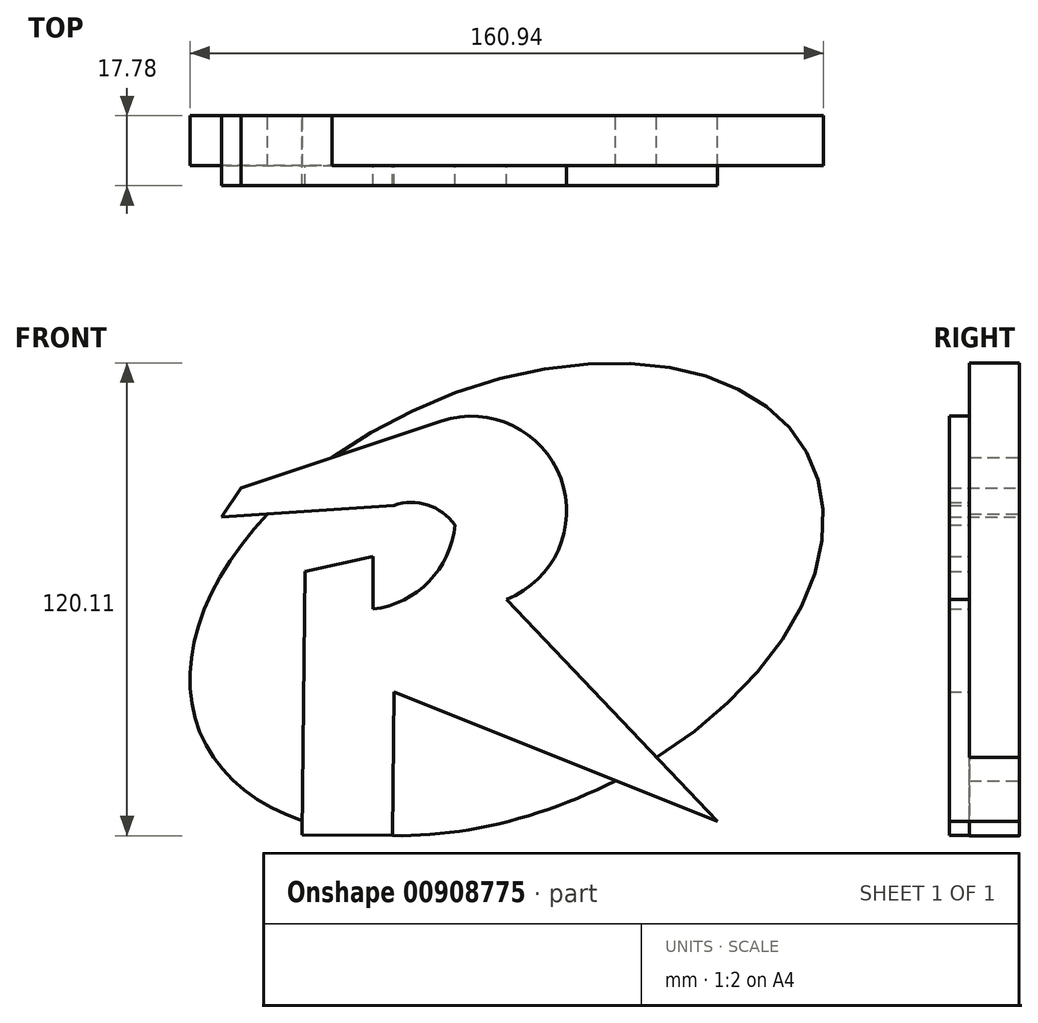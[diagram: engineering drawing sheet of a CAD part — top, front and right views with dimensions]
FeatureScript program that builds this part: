
annotation { "Feature Type Name" : "Feature", "Feature Type Description" : "" }
export const myFeature = defineFeature(function(context is Context, id is Id, definition is map)
    precondition{}
    {
        {
            var Q0;
            Q0=qCreatedBy(makeId("Front.planeOp"),FACE);
            var sketch = newSketch(context, id + "F0", { "sketchPlane" : qUnion([Q0])});
            skEllipse(sketch, "E0", {"center": v(0, 8.22) * mm, "majorRadius": 84.94 * mm, "minorRadius": 53.54 * mm, "majorAxis": v(-0.91, -0.41)});
            skLineSegment(sketch, "E1", {"start": v(-51.94, -51.6) * mm, "end": v(-29.03, -51.82) * mm});
            skLineSegment(sketch, "E2", {"start": v(-51.94, -51.6) * mm, "end": v(-51.3, 15.35) * mm});
            skLineSegment(sketch, "E3", {"start": v(-51.3, 15.35) * mm, "end": v(-33.96, 19.07) * mm});
            skLineSegment(sketch, "E4", {"start": v(-33.96, 19.07) * mm, "end": v(-33.96, 5.74) * mm});
            skArc(sketch, "E5", {"start": v(-33.96, 5.74) * mm, "mid": v(-19.76, 12.74) * mm, "end": v(-13.18, 27.14) * mm});
            skArc(sketch, "E6", {"start": v(-13.18, 27.14) * mm, "mid": v(-20.12, 32.17) * mm, "end": v(-28.69, 32.1) * mm});
            skLineSegment(sketch, "E7", {"start": v(-28.69, 32.1) * mm, "end": v(-72.41, 29.17) * mm});
            skLineSegment(sketch, "E8", {"start": v(-72.41, 29.17) * mm, "end": v(-67.45, 36.44) * mm});
            skLineSegment(sketch, "E9", {"start": v(-67.45, 36.44) * mm, "end": v(-16.6, 53.5) * mm});
            skArc(sketch, "E10", {"start": v(0, 8.22) * mm, "mid": v(13.73, 38.93) * mm, "end": v(-16.6, 53.5) * mm});
            skLineSegment(sketch, "E11", {"start": v(0, 8.22) * mm, "end": v(53.5, -48.22) * mm});
            skLineSegment(sketch, "E12", {"start": v(-29.03, -51.82) * mm, "end": v(-28.67, -15.34) * mm});
            skLineSegment(sketch, "E13", {"start": v(-28.67, -15.34) * mm, "end": v(53.5, -48.22) * mm});
            skSolve(sketch);
        }
        {
            var Q0;
            {var subQ5=sQuery(id+"F0.wireOp",EDGE,"E3");Q0=makeQuery(id+"F0.imprint","IMPRINT",FACE,{"disambiguationData":[TD([[makeQuery(id+"F0.imprint","IMPRINT",EDGE,{"derivedFrom":subQ5}),-1.0]])]});}
            var Q1;
            {var subQ5=sQuery(id+"F0.wireOp",EDGE,"E8");Q1=makeQuery(id+"F0.imprint","IMPRINT",FACE,{"disambiguationData":[TD([[makeQuery(id+"F0.imprint","IMPRINT",EDGE,{"derivedFrom":subQ5}),-1.0]])]});}
            var Q2;
            {var subQ0=sQuery(id+"F0.wireOp",EDGE,"E13");var subQ1=sQuery(id+"F0.wireOp",EDGE,"E0");var subQ2=makeQuery(id+"F0.imprint","INTERSECT",VERTEX,{"derivedFrom":[subQ1,subQ0]});Q2=makeQuery(id+"F0.imprint","IMPRINT",FACE,{"disambiguationData":[TD([[makeQuery(id+"F0.imprint","IMPRINT",EDGE,{"disambiguationData":[TD([[subQ2,-1.0]])],"derivedFrom":subQ1}),-1.0]])]});}
            var Q3;
            {var subQ0=sQuery(id+"F0.wireOp",EDGE,"E1");Q3=makeQuery(id+"F0.imprint","IMPRINT",FACE,{"disambiguationData":[TD([[makeQuery(id+"F0.imprint","IMPRINT",EDGE,{"derivedFrom":subQ0}),1.0]])]});}
            extrude(context, id + "F1", {"entities" : qUnion([Q0, Q1, Q2, Q3]), "depth" : 17.78 * mm, "offsetDistance" : 25.4 * mm});
        }
        {
            var Q0;
            {var subQ0=sQuery(id+"F0.wireOp",EDGE,"E3");Q0=makeQuery(id+"F0.imprint","IMPRINT",FACE,{"disambiguationData":[TD([[makeQuery(id+"F0.imprint","IMPRINT",EDGE,{"derivedFrom":subQ0}),1.0]])]});}
            var Q1;
            {var subQ0=sQuery(id+"F0.wireOp",EDGE,"E12");Q1=makeQuery(id+"F0.imprint","IMPRINT",FACE,{"disambiguationData":[TD([[makeQuery(id+"F0.imprint","IMPRINT",EDGE,{"derivedFrom":subQ0}),-1.0]])]});}
            var Q2;
            {var subQ5=sQuery(id+"F0.wireOp",EDGE,"E10");Q2=makeQuery(id+"F0.imprint","IMPRINT",FACE,{"disambiguationData":[TD([[makeQuery(id+"F0.imprint","IMPRINT",EDGE,{"derivedFrom":subQ5}),-1.0]])]});}
            extrude(context, id + "F2", {"entities" : qUnion([Q0, Q1, Q2]), "operationType" : NewBodyOperationType.ADD, "depth" : 12.7 * mm, "offsetDistance" : 25.4 * mm});
        }
    });
